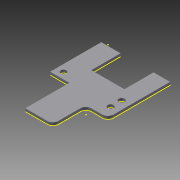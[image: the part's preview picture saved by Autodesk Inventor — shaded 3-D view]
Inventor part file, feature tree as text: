
AUTODESK INVENTOR PART (.ipt)
format: ipt  version: 2013 (Build 170138000, 138)  size: 260,096 bytes
history: native  units: in
note: dims shown in document units (in); Inventor stores cm internally (conversion verified against a paired STEP export)
features: sketch x17, extrude x9, other x8, sheet_metal_op x6, reference x6, chamfer x1
ambient origin geometry x8: Origin, YZ Plane, XZ Plane, XY Plane, X Axis, Y Axis, Z Axis, Center Point
bodies: Solid1 (feature_tree)
feature tree (47):
  sheet_metal_op  "Face1"
  sheet_metal_op  "Flange1"
  extrude  "Extrusion1"  Depth=0.125in
  sketch  "Sketch7"  dims[d10=0.125in d11=2.0in d12=0.0in]
  sketch  "Sketch8"  dims[d19=1.3125in d20=2.1in]
  sketch  "Sketch9"  dims[d21=0.25in d22=0.125in]
  extrude  "Extrusion4"  Depth=0.25in
  extrude  "Extrusion5"  Depth=1.0in TaperAngle=90.0deg
  extrude  "Extrusion6"  Depth=0.125in
  extrude  "Extrusion7"  Depth=2.0in TaperAngle=0.0deg
  extrude  "Extrusion8"  Depth=2.1in
  extrude  "Extrusion9"  Depth=0.125in
  sheet_metal_op  "Face2"
  chamfer  "Corner Round1"
  extrude  "Extrusion10"  Depth=0.125in TaperAngle=0.0deg
  extrude  "Extrusion11"  Depth=0.125in TaperAngle=0.0deg
  sketch  "Sketch24"  dims[d72=0.25in d73=0.125in d74=0.75in d75=0.125in d76=0.0in d77=0.125in d78=0.0in d79=0.25in d83=1.5in d84=0.0in d85=0.125in d86=0.0in d87=1.5in d88=0.0in]
  sketch  "Sketch1"  dims[d0=0.125in d1=0.125in]
  other  "Plate1"
  sketch  "Sketch2"  dims[d2=0.0625in d3=0.25in]
  other  "Plate2"
  sheet_metal_op  "Bend1"
  sheet_metal_op  "Corner1"
  sketch  "Sketch3"  dims[d4=0.125in d5=1.0in d6=90.0deg d7=0.05in]
  sketch  "Sketch6"  dims[d8=0.5in d9=0.125in]
  reference  "Reference1"
  sketch  "Sketch10"  dims[d23=0.0in d24=0.125in d25=0.0in]
  sketch  "Sketch15"  dims[d26=0.125in d27=0.0in d28=0.125in d29=0.0in]
  sketch  "Sketch16"  dims[d30=0.5in d31=0.0in]
  sketch  "Sketch17"  dims[d64=1.0in]
  reference  "Reference2"
  reference  "Reference3"
  reference  "Reference4"
  other  "Plate6"
  sheet_metal_op  "Bend5"
  sketch  "Sketch18"  dims[d65=2.0in d66=0.0in]
  sketch  "Sketch19"  dims[d67=2.0in d68=0.0in]
  reference  "Reference5"
  reference  "Reference6"
  sketch  "Sketch20"  dims[d69=0.125in]
  sketch  "Sketch22"  dims[d70=0.125in]
  sketch  "Sketch23"  dims[d71=0.0625in]
  other  "Cut1"
  other  "Cut3"
  other  "Cut4"
  other  "Cut5"
  other  "Definition1"
